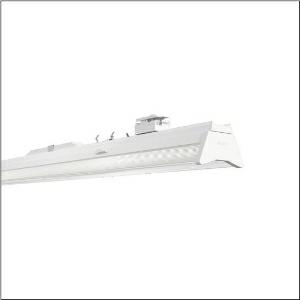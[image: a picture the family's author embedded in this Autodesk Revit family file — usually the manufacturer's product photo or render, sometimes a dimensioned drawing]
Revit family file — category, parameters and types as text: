
# Revit family: licross_r__21_performance_ho_52tm16mn4e5m_7be5
name_source: partatom
category: Lighting Fixtures
units: mm (PartAtom-declared; Revit-internal decimal feet)

## family parameters
Cut with Voids When Loaded = No
Host = Face
Light Source = No
Part Type = Normal
Room Calculation Point = No
Round Connector Dimension = Use Diameter
Shared = No

## types (1)
- --- (1 x LED, 14970 lm, 83.2 W, 4000K)
    Apparent Load = 83 VA
    CIE Flux Codes = 63 87 95 78 100
    Color Rendering = 80
    Color Temperature = 4000K
    Default Elevation = 1800 mm
    Description = Licross® 21 Performance HO, luminaire insert, of sheet steel, galvanised, coil coated, white, length: 1.500mm, width: 120mm, height: 123mm, LED rated luminous flux: 14.970lm, light colour: 840, control gear: ON/OFF Multilumen, with plug, 3-pole, with phase selection, mains connection: 220..240V, AC, 50/60Hz, rated input power: 83W, internal wiring halogen-free, primary light control with lens, of plastic, primary optical cover: cover, of PMMA, light emission: direct/indirect distribution, primary light characteristic: symmetric, protection rating (complete): IP40, insulation class (complete): insulation class I (protective earthing), certification: CE, ENEC, UKCA, protection symbol: D if used in an environment without relevant dust loads with corresponding accessories, impact resistance: IK06, permissible ambient temperature for indoor applications: -35..+35°C, corresponds to IFS (International Featured Standards) requirements for safety and quality in the food industry, reducing of maximum allowable ambient temperature of 5°C with ceiling mounting, LABS conformity tested according to VDMA 24364:2018-05, packaging unit: 1 piece
    Height = 114 mm
    Lamp = 1 x LED
    Lamp Light Flux = 14970 lm
    Lamp Power = 83.2 W
    Lamp count = 1
    Length = 1500 mm
    Luminous efficacy = 180 lm/W
    Manufacturer = Siteco
    ModVariant = No
    Model = 52TM16MN4E5M
    Mounting Place = Ceiling
    Mounting Type = Pendant
    Number of Poles = 1
    OnlyDefault = Yes
    Power Factor = 1
    Product Name = Licross® 21 Performance HO
    Product group = luminaire insert | ceiling pendant
    ProductGroupID = 902
    Protection Class = Protection class I
    Protection Degree = IP 40
    RLX_Detail_Level = 1
    RLX_Emergency_Light_Flux = 0 lm
    RLX_Emergency_Type = 0
    RLX_Emergency_Type_DB = No
    RlxData = <blob elided: 31793 chars, md5=2c8c7cdf>
    Socket = socket
    Standby Power = 0 W
    System Light Flux = 14970 lm
    System Power = 83 W
    Type Comments = factory setting: luminous flux: 100 % | (A | C | E) | 195 mA
    Type Image = l_1256138.jpg
    URL = http://relux.com
    VarID = @adj_130689
    Voltage = 0 V
    Weight = 0.00 kg
    Width = 120 mm

## geometry (parser evidence)
native form markers: Blend x4, Sweep x10
no freeform markers — native parametric forms only
